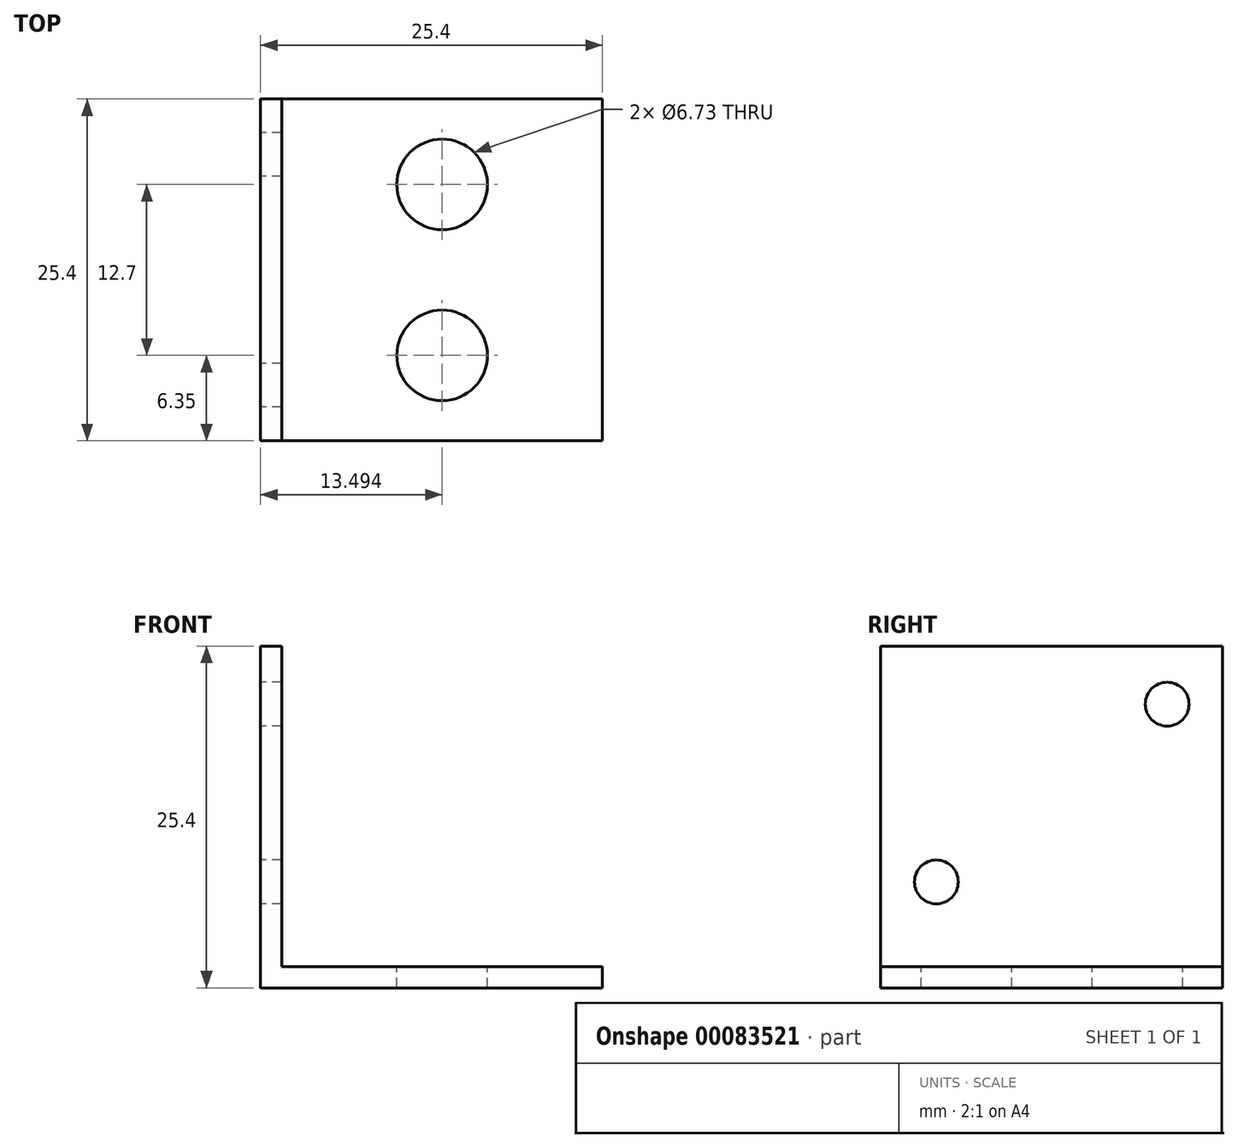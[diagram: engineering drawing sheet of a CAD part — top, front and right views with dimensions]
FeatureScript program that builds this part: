
annotation { "Feature Type Name" : "Feature", "Feature Type Description" : "" }
export const myFeature = defineFeature(function(context is Context, id is Id, definition is map)
    precondition{}
    {
        {
            var Q0;
            Q0=qCreatedBy(makeId("Front.planeOp"),FACE);
            var sketch = newSketch(context, id + "F0", { "sketchPlane" : qUnion([Q0])});
            skLineSegment(sketch, "E0", {"start": v(0, 25.4) * mm, "end": v(0, 0) * mm});
            skLineSegment(sketch, "E1", {"start": v(0, 0) * mm, "end": v(25.4, 0) * mm});
            skLineSegment(sketch, "E2", {"start": v(0, 25.4) * mm, "end": v(1.59, 25.4) * mm});
            skLineSegment(sketch, "E3", {"start": v(1.59, 25.4) * mm, "end": v(1.59, 1.59) * mm});
            skLineSegment(sketch, "E4", {"start": v(1.59, 1.59) * mm, "end": v(25.4, 1.59) * mm});
            skLineSegment(sketch, "E5", {"start": v(25.4, 1.59) * mm, "end": v(25.4, 0) * mm});
            skSolve(sketch);
        }
        {
            var Q0;
            Q0=makeQuery(id+"F0.imprint","IMPRINT",FACE,{"disambiguationData":[TD([[makeQuery(id+"F0.imprint","IMPRINT",EDGE,{"derivedFrom":sQuery(id+"F0.wireOp",EDGE,"E0")}),1.0]])]});
            extrude(context, id + "F1", {"entities" : qUnion([Q0]), "depth" : 25.4 * mm});
        }
        {
            var Q0;
            Q0=makeQuery(id+"F1.opExtrude","SWEPT_FACE",FACE,{"disambiguationData":[OSD([sQuery(id+"F0.wireOp",EDGE,"E0")])]});
            var sketch = newSketch(context, id + "F2", { "sketchPlane" : qUnion([Q0])});
            skPoint(sketch, "E6", {"position": v(4.13, 21.08) * mm});
            skPoint(sketch, "E7", {"position": v(21.27, 7.87) * mm});
            skLineSegment(sketch, "E8", {"start": v(4.13, 21.08) * mm, "end": v(4.13, 7.87) * mm});
            skLineSegment(sketch, "E9", {"start": v(21.27, 7.87) * mm, "end": v(4.13, 7.87) * mm});
            skLineSegment(sketch, "E10", {"start": v(12.7, 27.11) * mm, "end": v(12.7, -2.5) * mm});
            skPoint(sketch, "E10.startSnap0", {"position": v(12.7, 25.4) * mm});
            skSolve(sketch);
        }
        {
            var Q0;
            Q0=sQuery(id+"F2.wireOp",VERTEX,"E6");
            var Q1;
            Q1=sQuery(id+"F2.wireOp",VERTEX,"E7");
            var Q2;
            Q2=makeQuery(id+"F1.opExtrude","SWEPT_BODY",BODY,{"disambiguationData":[OSD([sQuery(id+"F0.wireOp",EDGE,"E0"),sQuery(id+"F0.wireOp",EDGE,"E1"),sQuery(id+"F0.wireOp",EDGE,"E2"),sQuery(id+"F0.wireOp",EDGE,"E3"),sQuery(id+"F0.wireOp",EDGE,"E4"),sQuery(id+"F0.wireOp",EDGE,"E5")])]});
            hole(context, id + "F3", {"style" : HoleStyle.SIMPLE, "endStyle" : HoleEndStyle.THROUGH, "holeDiameter" : 3.25 * mm, "locations" : qUnion([Q0, Q1]), "scope" : qUnion([Q2]), "isTappedThrough" : true});
        }
        {
            var Q0;
            Q0=makeQuery(id+"F1.opExtrude","SWEPT_FACE",FACE,{"disambiguationData":[OSD([sQuery(id+"F0.wireOp",EDGE,"E4")])]});
            var sketch = newSketch(context, id + "F4", { "sketchPlane" : qUnion([Q0])});
            skLineSegment(sketch, "E11", {"start": v(13.5, 0) * mm, "end": v(13.5, -25.4) * mm, "construction": true});
            skPoint(sketch, "E11.startSnap0", {"position": v(13.5, 0) * mm});
            skLineSegment(sketch, "E12", {"start": v(1.59, -12.7) * mm, "end": v(25.4, -12.7) * mm, "construction": true});
            skPoint(sketch, "E12.startSnap0", {"position": v(13.5, -12.7) * mm});
            skCircle(sketch, "E13", {"center": v(13.5, -19.05) * mm, "radius": 3.37 * mm});
            skCircle(sketch, "E14", {"center": v(13.5, -6.35) * mm, "radius": 3.37 * mm});
            skSolve(sketch);
        }
        {
            var Q0;
            Q0 = qSketchRegion(id + "F4", true);
            extrude(context, id + "F5", {"entities" : qUnion([Q0]), "operationType" : NewBodyOperationType.REMOVE, "oppositeDirection" : true, "depth" : 25.4 * mm});
        }
    });
